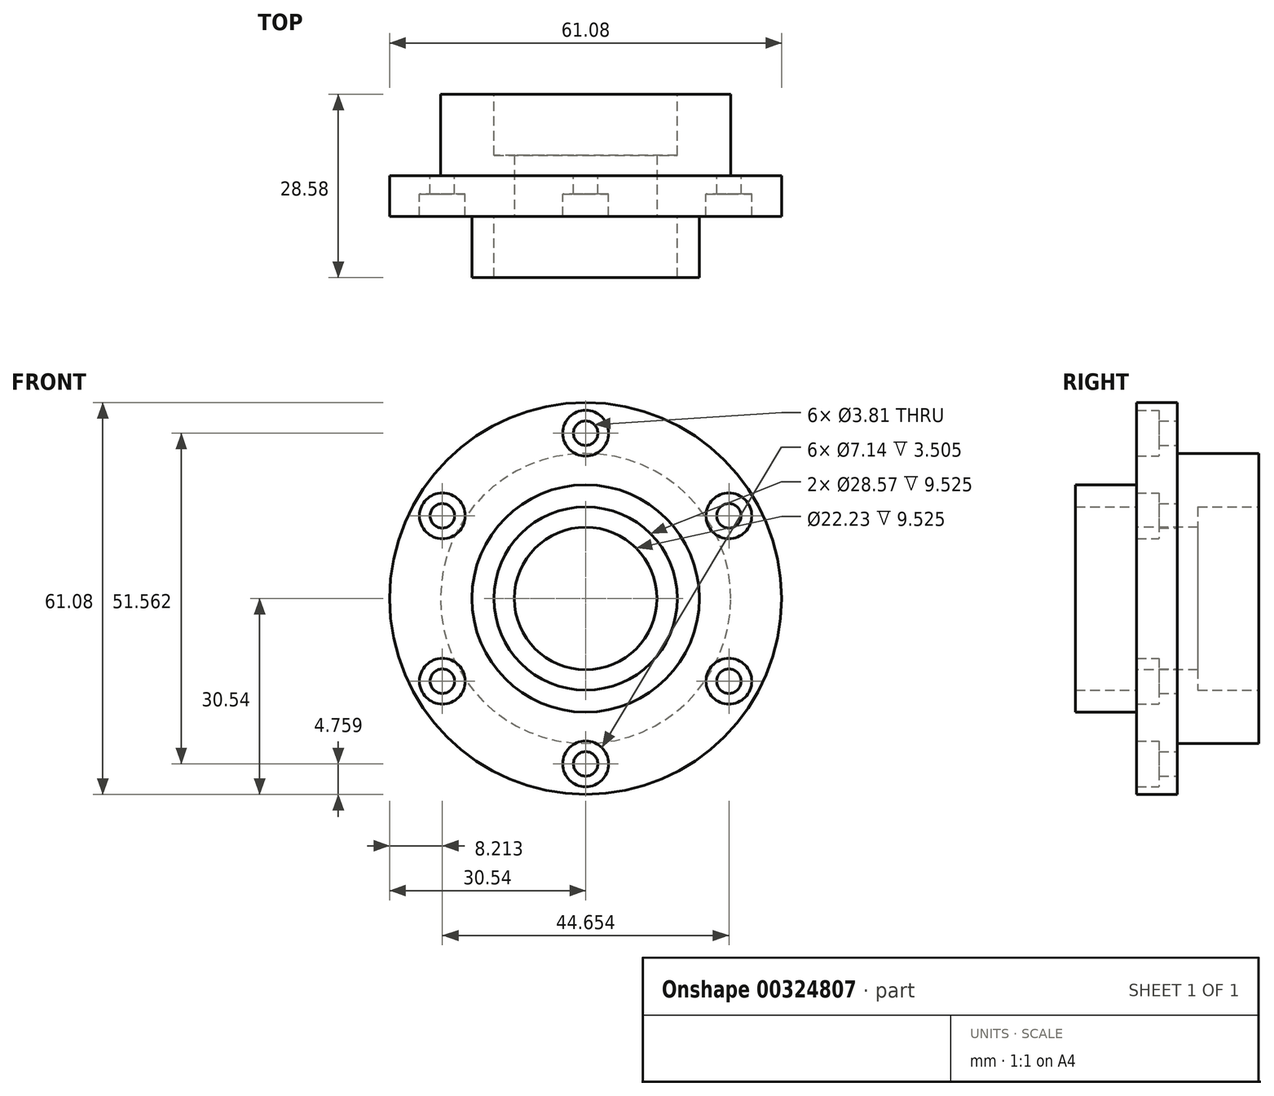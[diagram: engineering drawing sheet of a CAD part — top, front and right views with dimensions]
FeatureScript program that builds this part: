
annotation { "Feature Type Name" : "Feature", "Feature Type Description" : "" }
export const myFeature = defineFeature(function(context is Context, id is Id, definition is map)
    precondition{}
    {
        {
            var Q0;
            Q0=qCreatedBy(makeId("Front.planeOp"),FACE);
            var sketch = newSketch(context, id + "F0", { "sketchPlane" : qUnion([Q0])});
            skCircle(sketch, "E0", {"center": v(0, 0) * mm, "radius": 30.54 * mm});
            skSolve(sketch);
        }
        {
            var Q0;
            Q0=makeQuery(id+"F0.imprint","IMPRINT",FACE,{"disambiguationData":[TD([[makeQuery(id+"F0.imprint","IMPRINT",EDGE,{"derivedFrom":sQuery(id+"F0.wireOp",EDGE,"E0")}),1.0]])]});
            extrude(context, id + "F1", {"entities" : qUnion([Q0]), "depth" : 6.35 * mm});
        }
        {
            var Q0;
            Q0=makeQuery(id+"F1.opExtrude","CAP_FACE",FACE,{"disambiguationData":[OSD([sQuery(id+"F0.wireOp",EDGE,"E0")])],"isStart":false});
            var sketch = newSketch(context, id + "F2", { "sketchPlane" : qUnion([Q0])});
            skCircle(sketch, "E1", {"center": v(0, 0) * mm, "radius": 17.72 * mm});
            skCircle(sketch, "E2", {"center": v(0, 0) * mm, "radius": 14.29 * mm});
            skSolve(sketch);
        }
        {
            var Q0;
            Q0=makeQuery(id+"F2.imprint","IMPRINT",FACE,{"disambiguationData":[TD([[makeQuery(id+"F2.imprint","IMPRINT",EDGE,{"derivedFrom":sQuery(id+"F2.wireOp",EDGE,"E1")}),1.0]])]});
            extrude(context, id + "F3", {"entities" : qUnion([Q0]), "operationType" : NewBodyOperationType.ADD, "depth" : 9.52 * mm});
        }
        {
            var Q0;
            Q0=makeQuery(id+"F1.opExtrude","CAP_FACE",FACE,{"disambiguationData":[OSD([sQuery(id+"F0.wireOp",EDGE,"E0")])],"isStart":true});
            var sketch = newSketch(context, id + "F4", { "sketchPlane" : qUnion([Q0])});
            skCircle(sketch, "E3", {"center": v(0, 0) * mm, "radius": 22.6 * mm});
            skSolve(sketch);
        }
        {
            var Q0;
            Q0=makeQuery(id+"F4.imprint","IMPRINT",FACE,{"disambiguationData":[TD([[makeQuery(id+"F4.imprint","IMPRINT",EDGE,{"derivedFrom":sQuery(id+"F4.wireOp",EDGE,"E3")}),1.0]])]});
            extrude(context, id + "F5", {"entities" : qUnion([Q0]), "operationType" : NewBodyOperationType.ADD, "depth" : 12.7 * mm});
        }
        {
            var Q0;
            Q0=makeQuery(id+"F5.opExtrude","CAP_FACE",FACE,{"disambiguationData":[OSD([sQuery(id+"F4.wireOp",EDGE,"E3")])],"isStart":false});
            var sketch = newSketch(context, id + "F6", { "sketchPlane" : qUnion([Q0])});
            skCircle(sketch, "E4", {"center": v(0, 0) * mm, "radius": 14.29 * mm});
            skSolve(sketch);
        }
        {
            var Q0;
            Q0=makeQuery(id+"F6.imprint","IMPRINT",FACE,{"disambiguationData":[TD([[makeQuery(id+"F6.imprint","IMPRINT",EDGE,{"derivedFrom":sQuery(id+"F6.wireOp",EDGE,"E4")}),1.0]])]});
            extrude(context, id + "F7", {"entities" : qUnion([Q0]), "operationType" : NewBodyOperationType.REMOVE, "oppositeDirection" : true, "depth" : 9.52 * mm});
        }
        {
            var Q0;
            Q0=makeQuery(id+"F7.boolean.opBoolean","COPY",FACE,{"derivedFrom":makeQuery(id+"F7.opExtrude","CAP_FACE",FACE,{"disambiguationData":[OSD([sQuery(id+"F6.wireOp",EDGE,"E4")])],"isStart":false})});
            var sketch = newSketch(context, id + "F8", { "sketchPlane" : qUnion([Q0])});
            skCircle(sketch, "E5", {"center": v(0, 0) * mm, "radius": 11.11 * mm});
            skSolve(sketch);
        }
        {
            var Q0;
            Q0=makeQuery(id+"F8.imprint","IMPRINT",FACE,{"disambiguationData":[TD([[makeQuery(id+"F8.imprint","IMPRINT",EDGE,{"derivedFrom":sQuery(id+"F8.wireOp",EDGE,"E5")}),1.0]])]});
            extrude(context, id + "F9", {"entities" : qUnion([Q0]), "operationType" : NewBodyOperationType.REMOVE, "depth" : 38.1 * mm, "symmetric" : true});
        }
        {
            var Q0;
            {var subQ0=sQuery(id+"F0.wireOp",EDGE,"E0");Q0=makeQuery(id+"F3.boolean.opBoolean","SPLIT",FACE,{"disambiguationData":[TD([makeQuery(id+"F1.opExtrude","SWEPT_FACE",FACE,{"disambiguationData":[OSD([subQ0])]})])],"derivedFrom":makeQuery(id+"F1.opExtrude","CAP_FACE",FACE,{"disambiguationData":[OSD([subQ0])],"isStart":false})});}
            var sketch = newSketch(context, id + "F10", { "sketchPlane" : qUnion([Q0])});
            skPoint(sketch, "E6", {"position": v(0, 25.78) * mm});
            skPoint(sketch, "E7.1.0", {"position": v(-22.33, -12.9) * mm});
            skPoint(sketch, "E7.2.0", {"position": v(22.33, -12.9) * mm});
            skPoint(sketch, "E7.center", {"position": v(0, 0) * mm});
            skPoint(sketch, "E8.1.0", {"position": v(-22.33, 12.9) * mm});
            skPoint(sketch, "E9.0.3.0", {"position": v(0, -25.78) * mm});
            skPoint(sketch, "E9.0.5.0", {"position": v(22.33, 12.9) * mm});
            skSolve(sketch);
        }
        {
            var Q0;
            Q0=sQuery(id+"F10.wireOp",VERTEX,"E6");
            var Q1;
            Q1=sQuery(id+"F10.wireOp",VERTEX,"E8.1.0");
            var Q2;
            Q2=sQuery(id+"F10.wireOp",VERTEX,"E7.1.0");
            var Q3;
            Q3=sQuery(id+"F10.wireOp",VERTEX,"E9.0.3.0");
            var Q4;
            Q4=sQuery(id+"F10.wireOp",VERTEX,"E7.2.0");
            var Q5;
            Q5=sQuery(id+"F10.wireOp",VERTEX,"E9.0.5.0");
            var Q6;
            Q6=makeQuery(id+"F1.opExtrude","SWEPT_BODY",BODY,{"disambiguationData":[OSD([sQuery(id+"F0.wireOp",EDGE,"E0")])]});
            hole(context, id + "F11", {"style" : HoleStyle.C_BORE, "endStyle" : HoleEndStyle.THROUGH, "holeDiameter" : 3.8 * mm, "cBoreDiameter" : 7.14 * mm, "cBoreDepth" : 3.5 * mm, "tappedDepth" : 12.7 * mm, "tapClearance" : 3, "locations" : qUnion([Q0, Q1, Q2, Q3, Q4, Q5]), "scope" : qUnion([Q6])});
        }
    });
